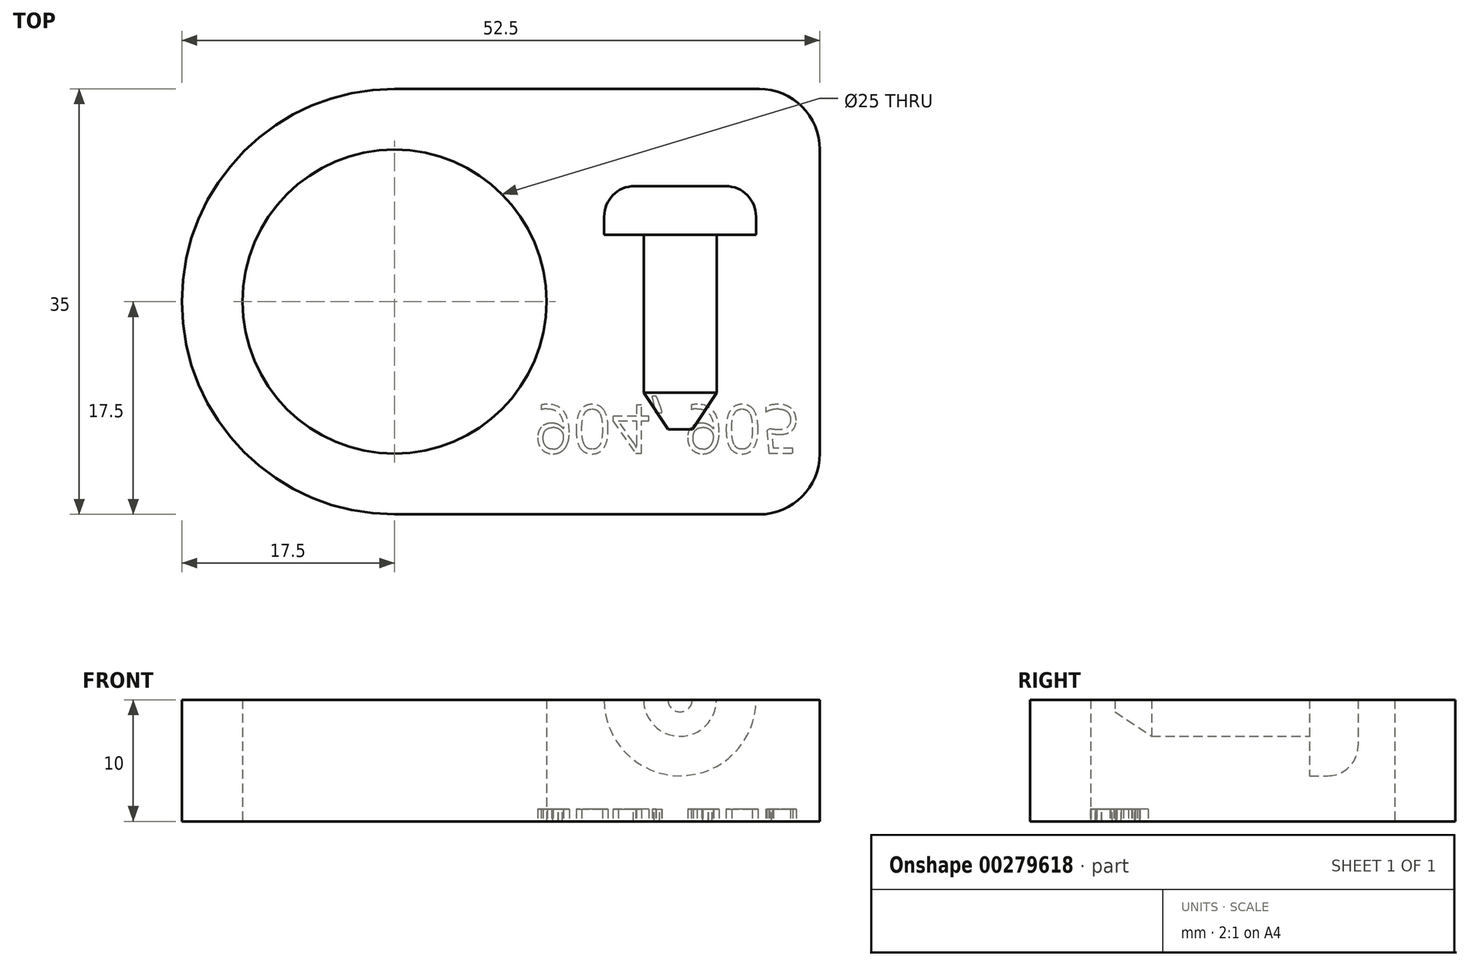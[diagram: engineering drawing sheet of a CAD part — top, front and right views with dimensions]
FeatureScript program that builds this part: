
annotation { "Feature Type Name" : "Feature", "Feature Type Description" : "" }
export const myFeature = defineFeature(function(context is Context, id is Id, definition is map)
    precondition{}
    {
        {
            var Q0;
            Q0=qCreatedBy(makeId("Top.planeOp"),FACE);
            var sketch = newSketch(context, id + "F0", { "sketchPlane" : qUnion([Q0])});
            skLineSegment(sketch, "E0.bottom", {"start": v(17.5, 0) * mm, "end": v(47.5, 0) * mm});
            skLineSegment(sketch, "E0.top", {"start": v(17.5, 35) * mm, "end": v(47.5, 35) * mm});
            skLineSegment(sketch, "E0.left", {"start": v(0, 17.5) * mm, "end": v(0, 17.5) * mm});
            skLineSegment(sketch, "E0.right", {"start": v(52.5, 5) * mm, "end": v(52.5, 30) * mm});
            skLineSegment(sketch, "E1.bottom", {"start": v(0, 0) * mm, "end": v(17.5, 0) * mm, "construction": true});
            skLineSegment(sketch, "E1.top", {"start": v(0, 17.5) * mm, "end": v(17.5, 17.5) * mm, "construction": true});
            skLineSegment(sketch, "E1.left", {"start": v(0, 0) * mm, "end": v(0, 17.5) * mm, "construction": true});
            skLineSegment(sketch, "E1.right", {"start": v(17.5, 0) * mm, "end": v(17.5, 17.5) * mm, "construction": true});
            skCircle(sketch, "E2", {"center": v(17.5, 17.5) * mm, "radius": 12.5 * mm});
            skPoint(sketch, "E3.visualSharp", {"position": v(0, 0) * mm});
            skArc(sketch, "E3.filletArc", {"start": v(0, 17.5) * mm, "mid": v(5.13, 5.13) * mm, "end": v(17.5, 0) * mm});
            skPoint(sketch, "E4.visualSharp", {"position": v(0, 35) * mm});
            skArc(sketch, "E4.filletArc", {"start": v(17.5, 35) * mm, "mid": v(5.13, 29.87) * mm, "end": v(0, 17.5) * mm});
            skPoint(sketch, "E5.visualSharp", {"position": v(52.5, 35) * mm});
            skArc(sketch, "E5.filletArc", {"start": v(52.5, 30) * mm, "mid": v(51.04, 33.54) * mm, "end": v(47.5, 35) * mm});
            skPoint(sketch, "E6.visualSharp", {"position": v(52.5, 0) * mm});
            skArc(sketch, "E6.filletArc", {"start": v(47.5, 0) * mm, "mid": v(51.04, 1.46) * mm, "end": v(52.5, 5) * mm});
            skSolve(sketch);
        }
        {
            var Q0;
            Q0=makeQuery(id+"F0.imprint","IMPRINT",FACE,{"disambiguationData":[TD([[makeQuery(id+"F0.imprint","IMPRINT",EDGE,{"derivedFrom":sQuery(id+"F0.wireOp",EDGE,"E0.bottom")}),1.0]])]});
            extrude(context, id + "F1", {"entities" : qUnion([Q0]), "depth" : 10 * mm});
        }
        {
            var Q0;
            Q0=makeQuery(id+"F1.opExtrude","CAP_FACE",FACE,{"disambiguationData":[OSD([sQuery(id+"F0.wireOp",EDGE,"E0.bottom"),sQuery(id+"F0.wireOp",EDGE,"E0.top"),sQuery(id+"F0.wireOp",EDGE,"E0.right"),sQuery(id+"F0.wireOp",EDGE,"E2"),sQuery(id+"F0.wireOp",EDGE,"E3.filletArc"),sQuery(id+"F0.wireOp",EDGE,"E4.filletArc"),sQuery(id+"F0.wireOp",EDGE,"E5.filletArc"),sQuery(id+"F0.wireOp",EDGE,"E6.filletArc")])],"isStart":false});
            var sketch = newSketch(context, id + "F2", { "sketchPlane" : qUnion([Q0])});
            skLineSegment(sketch, "E7.bottom", {"start": v(0, 0) * mm, "end": v(41, 0) * mm, "construction": true});
            skLineSegment(sketch, "E7.top", {"start": v(0, 7) * mm, "end": v(41, 7) * mm, "construction": true});
            skLineSegment(sketch, "E7.left", {"start": v(0, 0) * mm, "end": v(0, 7) * mm, "construction": true});
            skLineSegment(sketch, "E7.right", {"start": v(41, 0) * mm, "end": v(41, 7) * mm, "construction": true});
            skLineSegment(sketch, "E8", {"start": v(41, 7) * mm, "end": v(41, 23) * mm});
            skLineSegment(sketch, "E9.bottom", {"start": v(44, 23) * mm, "end": v(47.25, 23) * mm});
            skLineSegment(sketch, "E9.top", {"start": v(41, 27) * mm, "end": v(44.75, 27) * mm});
            skLineSegment(sketch, "E9.left", {"start": v(41, 23) * mm, "end": v(41, 27) * mm});
            skLineSegment(sketch, "E9.right", {"start": v(47.25, 23) * mm, "end": v(47.25, 24.5) * mm});
            skPoint(sketch, "E10.visualSharp", {"position": v(47.25, 27) * mm});
            skArc(sketch, "E10.filletArc", {"start": v(47.25, 24.5) * mm, "mid": v(46.52, 26.27) * mm, "end": v(44.75, 27) * mm});
            skLineSegment(sketch, "E11", {"start": v(44, 23) * mm, "end": v(44, 10) * mm});
            skLineSegment(sketch, "E12", {"start": v(41, 7) * mm, "end": v(42, 7) * mm});
            skLineSegment(sketch, "E13", {"start": v(42, 7) * mm, "end": v(44, 10) * mm});
            skSolve(sketch);
        }
        {
            var Q0;
            Q0=makeQuery(id+"F2.imprint","IMPRINT",FACE,{"disambiguationData":[TD([[makeQuery(id+"F2.imprint","IMPRINT",EDGE,{"derivedFrom":sQuery(id+"F2.wireOp",EDGE,"E8")}),-1.0]])]});
            var Q1;
            Q1=sQuery(id+"F2.wireOp",EDGE,"E8");
            revolve(context, id + "F3", {"operationType" : NewBodyOperationType.REMOVE, "entities" : qUnion([Q0]), "axis" : qUnion([Q1]), "revolveType" : RevolveType.FULL, "oppositeDirection" : true});
        }
        {
            var Q0;
            Q0=makeQuery(id+"F1.opExtrude","CAP_FACE",FACE,{"disambiguationData":[OSD([sQuery(id+"F0.wireOp",EDGE,"E0.bottom"),sQuery(id+"F0.wireOp",EDGE,"E0.top"),sQuery(id+"F0.wireOp",EDGE,"E0.right"),sQuery(id+"F0.wireOp",EDGE,"E2"),sQuery(id+"F0.wireOp",EDGE,"E3.filletArc"),sQuery(id+"F0.wireOp",EDGE,"E4.filletArc"),sQuery(id+"F0.wireOp",EDGE,"E5.filletArc"),sQuery(id+"F0.wireOp",EDGE,"E6.filletArc")])],"isStart":true});
            var sketch = newSketch(context, id + "F4", { "sketchPlane" : qUnion([Q0])});
            skLineSegment(sketch, "E14.bottom", {"start": v(0, 0) * mm, "end": v(29, 0) * mm, "construction": true});
            skLineSegment(sketch, "E14.top", {"start": v(0, -5) * mm, "end": v(29, -5) * mm, "construction": true});
            skLineSegment(sketch, "E14.left", {"start": v(0, 0) * mm, "end": v(0, -5) * mm, "construction": true});
            skLineSegment(sketch, "E14.right", {"start": v(29, 0) * mm, "end": v(29, -5) * mm, "construction": true});
            skText(sketch, "E15", { "text": "904, 905", "fontName": "OpenSans-Regular.ttf"});
            const initialGuessF4  = {"E15": [0.029, -0.009, 1, 0, 0.004]};
            skSetInitialGuess(sketch, initialGuessF4);
            skSolve(sketch);
        }
        {
            var Q0;
            Q0 = qSketchRegion(id + "F4", true);
            extrude(context, id + "F5", {"entities" : qUnion([Q0]), "operationType" : NewBodyOperationType.REMOVE, "oppositeDirection" : true, "depth" : 1 * mm});
        }
    });
